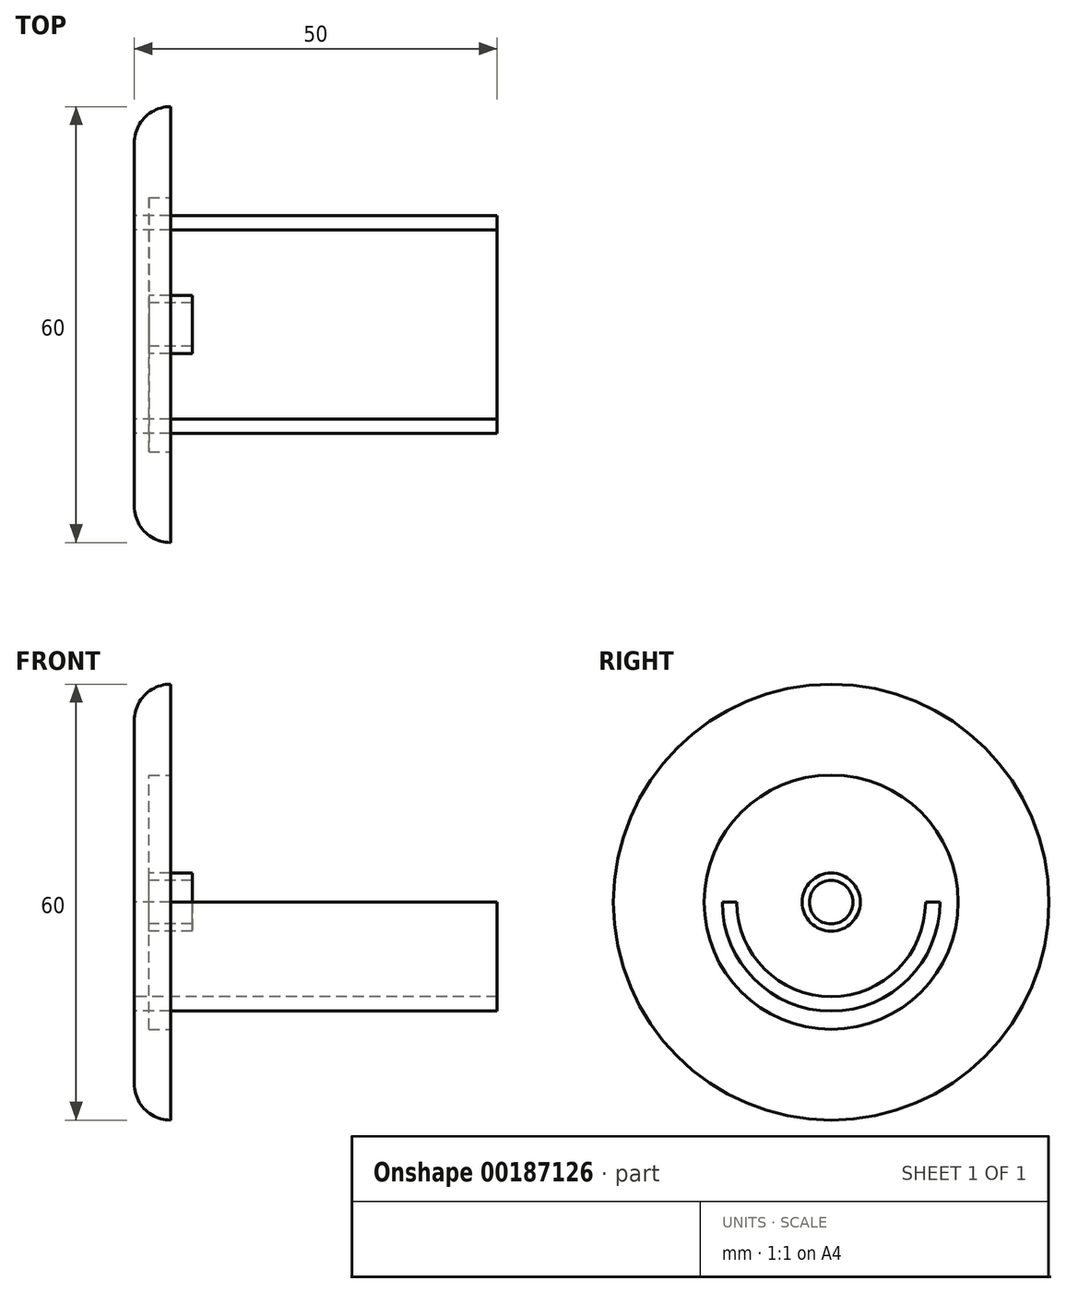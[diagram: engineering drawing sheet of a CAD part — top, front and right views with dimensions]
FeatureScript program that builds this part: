
annotation { "Feature Type Name" : "Feature", "Feature Type Description" : "" }
export const myFeature = defineFeature(function(context is Context, id is Id, definition is map)
    precondition{}
    {
        {
            var Q0;
            Q0=qCreatedBy(makeId("Right.planeOp"),FACE);
            var sketch = newSketch(context, id + "F0", { "sketchPlane" : qUnion([Q0])});
            skCircle(sketch, "E0", {"center": v(0, 0) * mm, "radius": 30 * mm});
            skSolve(sketch);
        }
        {
            var Q0;
            Q0=makeQuery(id+"F0.imprint","IMPRINT",FACE,{"disambiguationData":[TD([[makeQuery(id+"F0.imprint","IMPRINT",EDGE,{"derivedFrom":sQuery(id+"F0.wireOp",EDGE,"E0")}),1.0]])]});
            extrude(context, id + "F1", {"entities" : qUnion([Q0]), "depth" : 5 * mm});
        }
        {
            var Q0;
            Q0=makeQuery(id+"F1.opExtrude","CAP_EDGE",EDGE,{"disambiguationData":[OSD([sQuery(id+"F0.wireOp",EDGE,"E0")])],"isStart":true});
            fillet(context, id + "F2", {"entities" : qUnion([Q0]), "radius" : 5 * mm, "tangentPropagation" : true, "allowEdgeOverflow" : false});
        }
        {
            var Q0;
            Q0=makeQuery(id+"F1.opExtrude","CAP_FACE",FACE,{"disambiguationData":[OSD([sQuery(id+"F0.wireOp",EDGE,"E0")])],"isStart":false});
            var sketch = newSketch(context, id + "F3", { "sketchPlane" : qUnion([Q0])});
            skCircle(sketch, "E1", {"center": v(0, 0) * mm, "radius": 17.5 * mm});
            skSolve(sketch);
        }
        {
            var Q0;
            Q0=makeQuery(id+"F3.imprint","IMPRINT",FACE,{"disambiguationData":[TD([[makeQuery(id+"F3.imprint","IMPRINT",EDGE,{"derivedFrom":sQuery(id+"F3.wireOp",EDGE,"E1")}),1.0]])]});
            extrude(context, id + "F4", {"entities" : qUnion([Q0]), "operationType" : NewBodyOperationType.REMOVE, "oppositeDirection" : true, "depth" : 3 * mm});
        }
        {
            var Q0;
            Q0=makeQuery(id+"F4.boolean.opBoolean","COPY",FACE,{"derivedFrom":makeQuery(id+"F4.opExtrude","CAP_FACE",FACE,{"disambiguationData":[OSD([sQuery(id+"F3.wireOp",EDGE,"E1")])],"isStart":false})});
            var sketch = newSketch(context, id + "F5", { "sketchPlane" : qUnion([Q0])});
            skCircle(sketch, "E2", {"center": v(0, 0) * mm, "radius": 4 * mm});
            skCircle(sketch, "E3", {"center": v(0, 0) * mm, "radius": 3 * mm});
            skSolve(sketch);
        }
        {
            var Q0;
            Q0=makeQuery(id+"F5.imprint","IMPRINT",FACE,{"disambiguationData":[TD([[makeQuery(id+"F5.imprint","IMPRINT",EDGE,{"derivedFrom":sQuery(id+"F5.wireOp",EDGE,"E2")}),1.0]])]});
            extrude(context, id + "F6", {"entities" : qUnion([Q0]), "operationType" : NewBodyOperationType.ADD, "depth" : 6 * mm});
        }
        {
            var Q0;
            Q0=qCreatedBy(makeId("Right.planeOp"),FACE);
            var sketch = newSketch(context, id + "F7", { "sketchPlane" : qUnion([Q0])});
            skArc(sketch, "E4", {"start": v(-15, 0) * mm, "mid": v(0, -15) * mm, "end": v(15, 0) * mm});
            skArc(sketch, "E5.0", {"start": v(-13, 0) * mm, "mid": v(0, -13) * mm, "end": v(13, 0) * mm});
            skLineSegment(sketch, "E6", {"start": v(-13, 0) * mm, "end": v(-15, 0) * mm});
            skLineSegment(sketch, "E7", {"start": v(15, 0) * mm, "end": v(13, 0) * mm});
            skSolve(sketch);
        }
        {
            var Q0;
            Q0=makeQuery(id+"F7.imprint","IMPRINT",FACE,{"disambiguationData":[TD([[makeQuery(id+"F7.imprint","IMPRINT",EDGE,{"derivedFrom":sQuery(id+"F7.wireOp",EDGE,"E4")}),1.0]])]});
            extrude(context, id + "F8", {"entities" : qUnion([Q0]), "depth" : 50 * mm});
        }
    });
